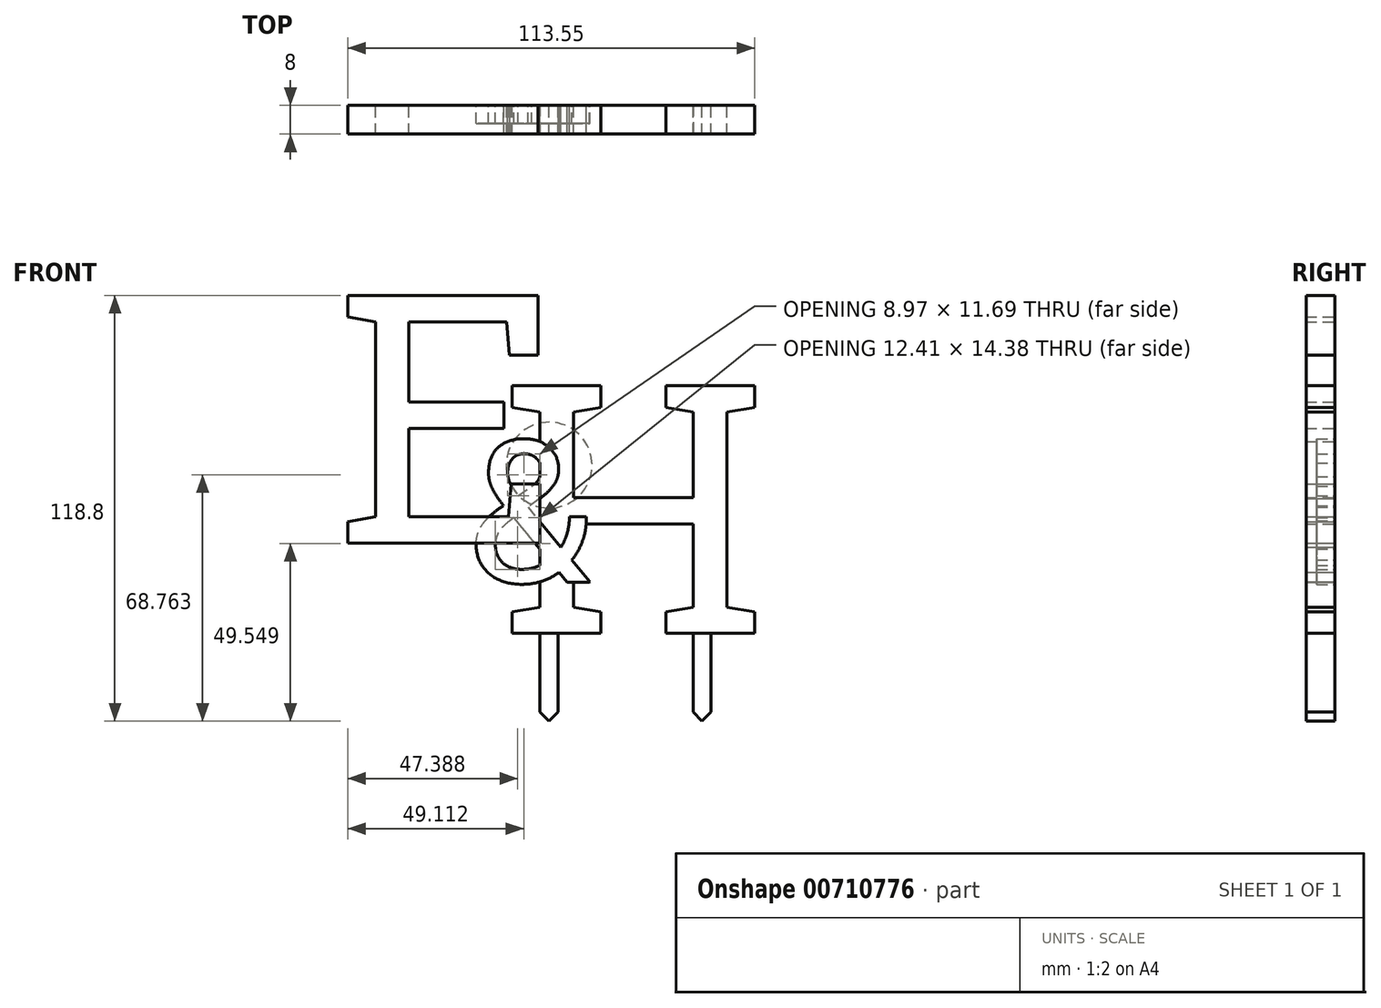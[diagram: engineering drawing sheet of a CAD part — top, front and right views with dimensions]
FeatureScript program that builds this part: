
annotation { "Feature Type Name" : "Feature", "Feature Type Description" : "" }
export const myFeature = defineFeature(function(context is Context, id is Id, definition is map)
    precondition{}
    {
        {
            var Q0;
            Q0=qCreatedBy(makeId("Front.planeOp"),FACE);
            var sketch = newSketch(context, id + "F0", { "sketchPlane" : qUnion([Q0])});
            skText(sketch, "E0", { "text": "E", "fontName": "RobotoSlab-Regular.ttf"});
            skText(sketch, "E1", { "text": "&", "fontName": "RobotoSlab-Regular.ttf"});
            skText(sketch, "E2", { "text": "H", "fontName": "RobotoSlab-Regular.ttf"});
            const initialGuessF0  = {"E0": [-0.21462, 0.00408, 1, 0, 0.07], "E1": [-0.17742, -0.00685, 1, 0, 0.04], "E2": [-0.16876, -0.0211, 1, 0, 0.07]};
            skSetInitialGuess(sketch, initialGuessF0);
            skSolve(sketch);
        }
        {
            var Q0;
            {var subQ7=sQuery(id+"F0.wireOp",EDGE,"E0.sketch_text.stroke-0");Q0=makeQuery(id+"F0.imprint","IMPRINT",FACE,{"disambiguationData":[TD([[makeQuery(id+"F0.imprint","IMPRINT",EDGE,{"derivedFrom":subQ7}),-1.0]])]});}
            var Q1;
            {var subQ0=sQuery(id+"F0.wireOp",EDGE,"E1.sketch_text.stroke-35");Q1=makeQuery(id+"F0.imprint","IMPRINT",FACE,{"disambiguationData":[TD([[makeQuery(id+"F0.imprint","IMPRINT",EDGE,{"derivedFrom":subQ0}),1.0]])]});}
            var Q2;
            {var subQ2=sQuery(id+"F0.wireOp",EDGE,"E1.sketch_text.stroke-20");Q2=makeQuery(id+"F0.imprint","IMPRINT",FACE,{"disambiguationData":[TD([[makeQuery(id+"F0.imprint","IMPRINT",EDGE,{"derivedFrom":subQ2}),1.0]])]});}
            var Q3;
            {var subQ6=sQuery(id+"F0.wireOp",EDGE,"E1.sketch_text.stroke-7");Q3=makeQuery(id+"F0.imprint","IMPRINT",FACE,{"disambiguationData":[TD([[makeQuery(id+"F0.imprint","IMPRINT",EDGE,{"derivedFrom":subQ6}),1.0]])]});}
            var Q4;
            {var subQ1=sQuery(id+"F0.wireOp",EDGE,"E1.sketch_text.stroke-28");Q4=makeQuery(id+"F0.imprint","IMPRINT",FACE,{"disambiguationData":[TD([[makeQuery(id+"F0.imprint","IMPRINT",EDGE,{"derivedFrom":subQ1}),1.0]])]});}
            var Q5;
            {var subQ0=sQuery(id+"F0.wireOp",EDGE,"E1.sketch_text.stroke-10");Q5=makeQuery(id+"F0.imprint","IMPRINT",FACE,{"disambiguationData":[TD([[makeQuery(id+"F0.imprint","IMPRINT",EDGE,{"derivedFrom":subQ0}),1.0]])]});}
            var Q6;
            {var subQ1=sQuery(id+"F0.wireOp",EDGE,"E1.sketch_text.stroke-10");Q6=makeQuery(id+"F0.imprint","IMPRINT",FACE,{"disambiguationData":[TD([[makeQuery(id+"F0.imprint","IMPRINT",EDGE,{"derivedFrom":subQ1}),-1.0]])]});}
            extrude(context, id + "F1", {"entities" : qUnion([Q0, Q1, Q2, Q3, Q4, Q5, Q6]), "depth" : 8 * mm, "offsetDistance" : 25 * mm});
        }
        {
            var Q0;
            {var subQ5=sQuery(id+"F0.wireOp",EDGE,"E1.sketch_text.stroke-2");Q0=makeQuery(id+"F0.imprint","IMPRINT",FACE,{"disambiguationData":[TD([[makeQuery(id+"F0.imprint","IMPRINT",EDGE,{"derivedFrom":subQ5}),-1.0]])]});}
            var Q1;
            {var subQ0=sQuery(id+"F0.wireOp",EDGE,"E1.sketch_text.stroke-7");Q1=makeQuery(id+"F0.imprint","IMPRINT",FACE,{"disambiguationData":[TD([[makeQuery(id+"F0.imprint","IMPRINT",EDGE,{"derivedFrom":subQ0}),-1.0]])]});}
            var Q2;
            {var subQ1=sQuery(id+"F0.wireOp",EDGE,"E1.sketch_text.stroke-10");Q2=makeQuery(id+"F0.imprint","IMPRINT",FACE,{"disambiguationData":[TD([[makeQuery(id+"F0.imprint","IMPRINT",EDGE,{"derivedFrom":subQ1}),-1.0]])]});}
            var Q3;
            {var subQ11=sQuery(id+"F0.wireOp",EDGE,"E1.sketch_text.stroke-23");Q3=makeQuery(id+"F0.imprint","IMPRINT",FACE,{"disambiguationData":[TD([[makeQuery(id+"F0.imprint","IMPRINT",EDGE,{"derivedFrom":subQ11}),-1.0]])]});}
            var Q4;
            {var subQ26=sQuery(id+"F0.wireOp",EDGE,"E1.sketch_text.stroke-12");Q4=makeQuery(id+"F0.imprint","IMPRINT",FACE,{"disambiguationData":[TD([[makeQuery(id+"F0.imprint","IMPRINT",EDGE,{"derivedFrom":subQ26}),-1.0]])]});}
            var Q5;
            {var subQ0=sQuery(id+"F0.wireOp",EDGE,"E1.sketch_text.stroke-16");var subQ1=sQuery(id+"F0.wireOp",EDGE,"E1.sketch_text.stroke-15");var subQ2=makeQuery(id+"F0.imprint","INTERSECT",VERTEX,{"derivedFrom":[subQ1,subQ0]});Q5=makeQuery(id+"F0.imprint","IMPRINT",FACE,{"disambiguationData":[TD([[makeQuery(id+"F0.imprint","IMPRINT",EDGE,{"disambiguationData":[TD([[subQ2,1.0]])],"derivedFrom":subQ1}),-1.0]])]});}
            var Q6;
            {var subQ0=sQuery(id+"F0.wireOp",EDGE,"E1.sketch_text.stroke-27");var subQ1=sQuery(id+"F0.wireOp",EDGE,"E1.sketch_text.stroke-26");var subQ2=makeQuery(id+"F0.imprint","INTERSECT",VERTEX,{"derivedFrom":[subQ1,subQ0]});Q6=makeQuery(id+"F0.imprint","IMPRINT",FACE,{"disambiguationData":[TD([[makeQuery(id+"F0.imprint","IMPRINT",EDGE,{"disambiguationData":[TD([[subQ2,1.0]])],"derivedFrom":subQ1}),1.0]])]});}
            var Q7;
            {var subQ0=sQuery(id+"F0.wireOp",EDGE,"E2.sketch_text.stroke-28");var subQ1=sQuery(id+"F0.wireOp",EDGE,"E0.sketch_text.stroke-19");var subQ2=makeQuery(id+"F0.imprint","INTERSECT",VERTEX,{"derivedFrom":[subQ1,subQ0]});Q7=makeQuery(id+"F0.imprint","IMPRINT",FACE,{"disambiguationData":[TD([[makeQuery(id+"F0.imprint","IMPRINT",EDGE,{"disambiguationData":[TD([[subQ2,-1.0]])],"derivedFrom":subQ1}),1.0]])]});}
            var Q8;
            {var subQ0=sQuery(id+"F0.wireOp",EDGE,"E1.sketch_text.stroke-18");Q8=makeQuery(id+"F0.imprint","IMPRINT",FACE,{"disambiguationData":[TD([[makeQuery(id+"F0.imprint","IMPRINT",EDGE,{"derivedFrom":subQ0}),-1.0]])]});}
            var Q9;
            {var subQ0=sQuery(id+"F0.wireOp",EDGE,"E1.sketch_text.stroke-36");var subQ1=sQuery(id+"F0.wireOp",EDGE,"E0.sketch_text.stroke-17");var subQ2=makeQuery(id+"F0.imprint","INTERSECT",VERTEX,{"derivedFrom":[subQ1,subQ0]});Q9=makeQuery(id+"F0.imprint","IMPRINT",FACE,{"disambiguationData":[TD([[makeQuery(id+"F0.imprint","IMPRINT",EDGE,{"disambiguationData":[TD([[subQ2,-1.0]])],"derivedFrom":subQ1}),1.0]])]});}
            var Q10;
            {var subQ0=sQuery(id+"F0.wireOp",EDGE,"E1.sketch_text.stroke-38");var subQ1=sQuery(id+"F0.wireOp",EDGE,"E1.sketch_text.stroke-37");var subQ2=makeQuery(id+"F0.imprint","INTERSECT",VERTEX,{"derivedFrom":[subQ1,subQ0]});Q10=makeQuery(id+"F0.imprint","IMPRINT",FACE,{"disambiguationData":[TD([[makeQuery(id+"F0.imprint","IMPRINT",EDGE,{"disambiguationData":[TD([[subQ2,1.0]])],"derivedFrom":subQ1}),1.0]])]});}
            extrude(context, id + "F2", {"entities" : qUnion([Q0, Q1, Q2, Q3, Q4, Q5, Q6, Q7, Q8, Q9, Q10]), "depth" : 5 * mm, "offsetDistance" : 25 * mm});
        }
        {
            var Q0;
            Q0=makeQuery(id+"F1.opExtrude","SWEPT_FACE",FACE,{"disambiguationData":[OSD([sQuery(id+"F0.wireOp",EDGE,"E2.sketch_text.stroke-25")])]});
            var sketch = newSketch(context, id + "F3", { "sketchPlane" : qUnion([Q0])});
            skLineSegment(sketch, "E3.bottom", {"start": v(-157.6, 8) * mm, "end": v(-152.6, 8) * mm});
            skLineSegment(sketch, "E3.top", {"start": v(-157.6, 0) * mm, "end": v(-152.6, 0) * mm});
            skLineSegment(sketch, "E3.left", {"start": v(-157.6, 8) * mm, "end": v(-157.6, 0) * mm});
            skLineSegment(sketch, "E3.right", {"start": v(-152.6, 8) * mm, "end": v(-152.6, 0) * mm});
            skLineSegment(sketch, "E4.bottom", {"start": v(-114.88, 8) * mm, "end": v(-109.88, 8) * mm});
            skLineSegment(sketch, "E4.top", {"start": v(-114.88, 0) * mm, "end": v(-109.88, 0) * mm});
            skLineSegment(sketch, "E4.left", {"start": v(-114.88, 8) * mm, "end": v(-114.88, 0) * mm});
            skLineSegment(sketch, "E4.right", {"start": v(-109.88, 8) * mm, "end": v(-109.88, 0) * mm});
            skSolve(sketch);
        }
        {
            var Q0;
            Q0=makeQuery(id+"F3.imprint","IMPRINT",FACE,{"disambiguationData":[TD([[makeQuery(id+"F3.imprint","IMPRINT",EDGE,{"derivedFrom":sQuery(id+"F3.wireOp",EDGE,"E3.bottom")}),1.0]])]});
            var Q1;
            Q1=makeQuery(id+"F3.imprint","IMPRINT",FACE,{"disambiguationData":[TD([[makeQuery(id+"F3.imprint","IMPRINT",EDGE,{"derivedFrom":sQuery(id+"F3.wireOp",EDGE,"E4.bottom")}),-1.0]])]});
            extrude(context, id + "F4", {"entities" : qUnion([Q0, Q1]), "depth" : 25 * mm, "offsetDistance" : 25 * mm});
        }
        {
            var Q0;
            Q0=makeQuery(id+"F4.opExtrude","CAP_EDGE",EDGE,{"disambiguationData":[OSD([sQuery(id+"F3.wireOp",EDGE,"E3.left")])],"isStart":false});
            var Q1;
            Q1=makeQuery(id+"F4.opExtrude","CAP_EDGE",EDGE,{"disambiguationData":[OSD([sQuery(id+"F3.wireOp",EDGE,"E3.right")])],"isStart":false});
            var Q2;
            Q2=makeQuery(id+"F4.opExtrude","CAP_EDGE",EDGE,{"disambiguationData":[OSD([sQuery(id+"F3.wireOp",EDGE,"E4.left")])],"isStart":false});
            var Q3;
            Q3=makeQuery(id+"F4.opExtrude","CAP_EDGE",EDGE,{"disambiguationData":[OSD([sQuery(id+"F3.wireOp",EDGE,"E4.right")])],"isStart":false});
            chamfer(context, id + "F5", {"entities" : qUnion([Q0, Q1, Q2, Q3]), "width" : 3 * mm, "tangentPropagation" : true});
        }
    });
